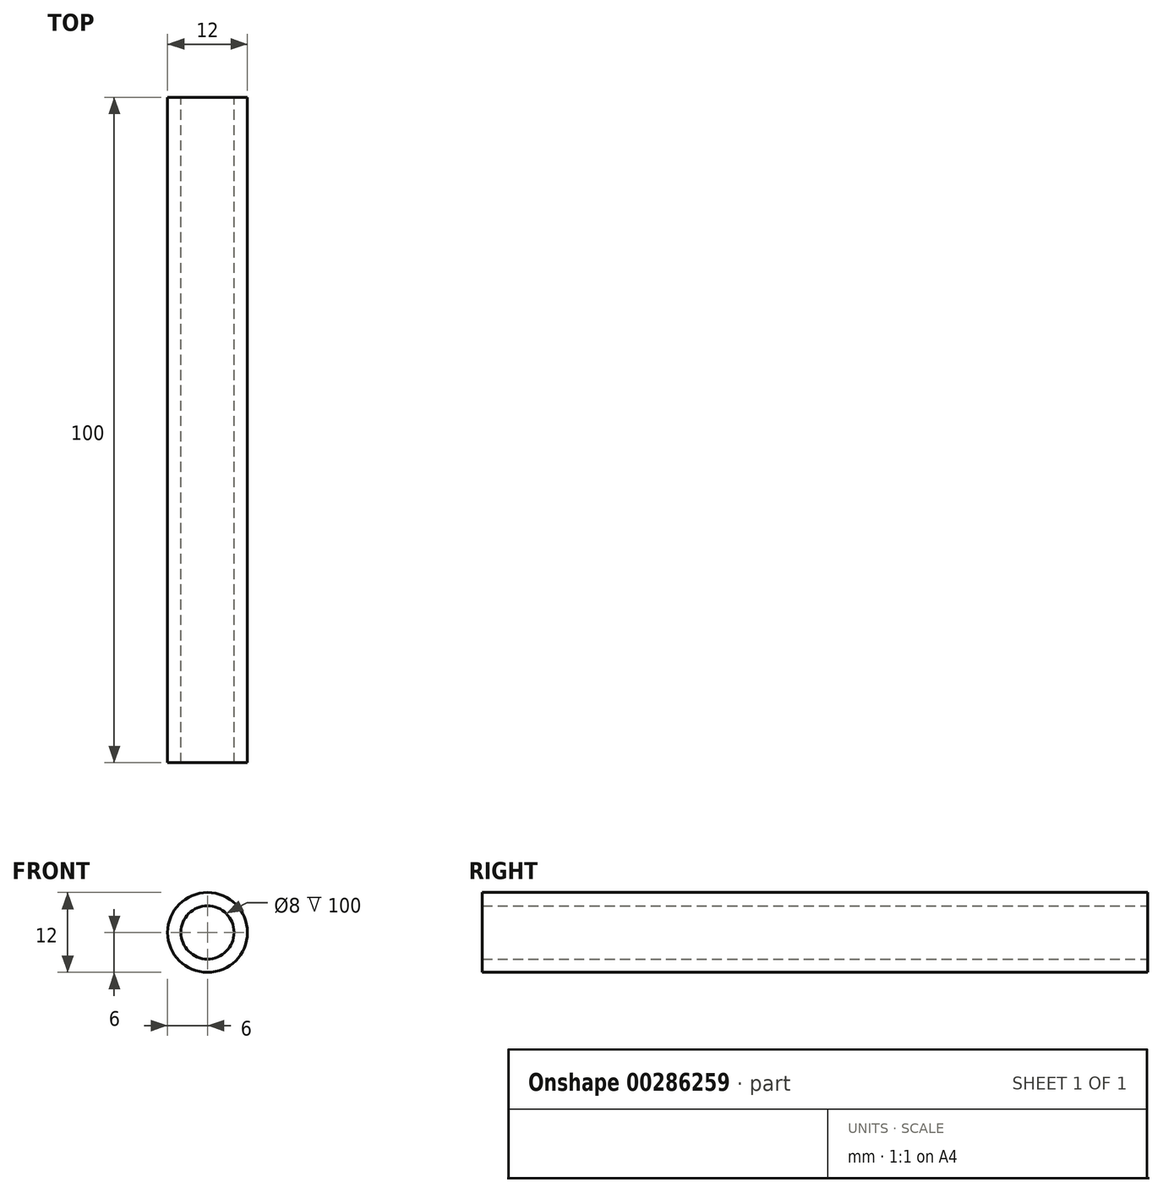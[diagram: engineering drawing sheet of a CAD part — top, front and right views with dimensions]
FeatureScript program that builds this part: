
annotation { "Feature Type Name" : "Feature", "Feature Type Description" : "" }
export const myFeature = defineFeature(function(context is Context, id is Id, definition is map)
    precondition{}
    {
        {
            var Q0;
            Q0=qCreatedBy(makeId("Front.planeOp"),FACE);
            var sketch = newSketch(context, id + "F0", { "sketchPlane" : qUnion([Q0])});
            skCircle(sketch, "E0", {"center": v(0, 0) * mm, "radius": 6 * mm});
            skCircle(sketch, "E1", {"center": v(0, 0) * mm, "radius": 4 * mm});
            skSolve(sketch);
        }
        {
            var Q0;
            Q0 = qSketchRegion(id + "F0", true);
            extrude(context, id + "F1", {"entities" : qUnion([Q0]), "depth" : 100 * mm});
        }
    });
